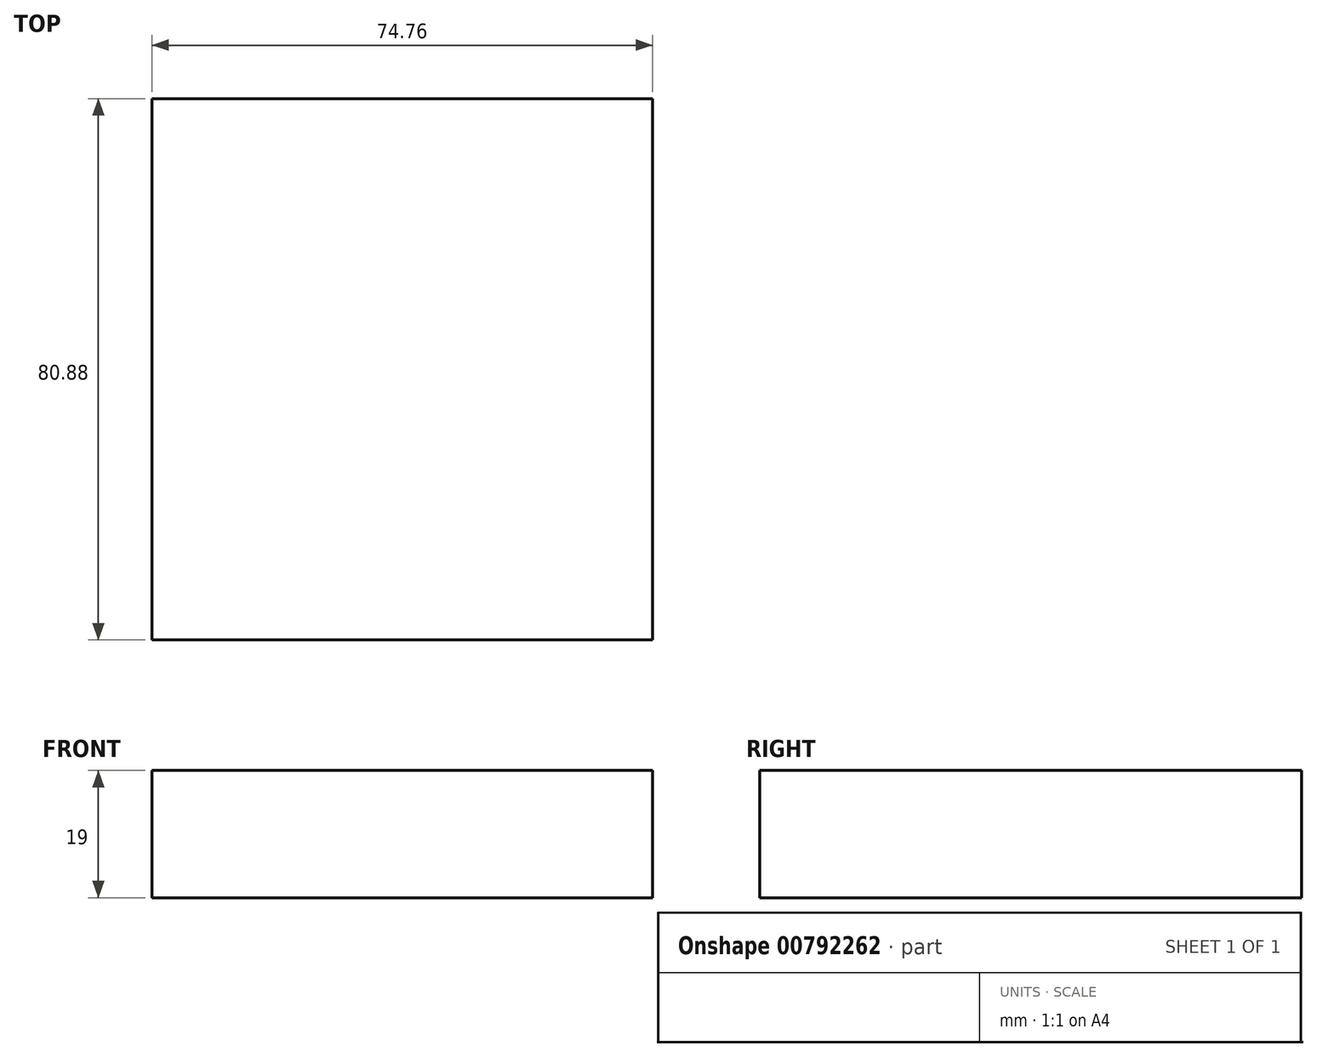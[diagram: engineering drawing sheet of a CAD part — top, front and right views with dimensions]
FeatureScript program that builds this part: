
annotation { "Feature Type Name" : "Feature", "Feature Type Description" : "" }
export const myFeature = defineFeature(function(context is Context, id is Id, definition is map)
    precondition{}
    {
        {
            var Q0;
            Q0=qCreatedBy(makeId("Top.planeOp"),FACE);
            var sketch = newSketch(context, id + "F0", { "sketchPlane" : qUnion([Q0])});
            skLineSegment(sketch, "E0.bottom", {"start": v(-37.97, 29.62) * mm, "end": v(36.79, 29.62) * mm});
            skLineSegment(sketch, "E0.top", {"start": v(-37.97, -51.26) * mm, "end": v(36.79, -51.26) * mm});
            skLineSegment(sketch, "E0.left", {"start": v(-37.97, 29.62) * mm, "end": v(-37.97, -51.26) * mm});
            skLineSegment(sketch, "E0.right", {"start": v(36.79, 29.62) * mm, "end": v(36.79, -51.26) * mm});
            skSolve(sketch);
        }
        {
            var Q0;
            Q0=makeQuery(id+"F0.imprint","IMPRINT",FACE,{"disambiguationData":[TD([[makeQuery(id+"F0.imprint","IMPRINT",EDGE,{"derivedFrom":sQuery(id+"F0.wireOp",EDGE,"E0.bottom")}),-1.0]])]});
            extrude(context, id + "F1", {"entities" : qUnion([Q0]), "depth" : 19 * mm, "offsetDistance" : 25 * mm});
        }
    });
